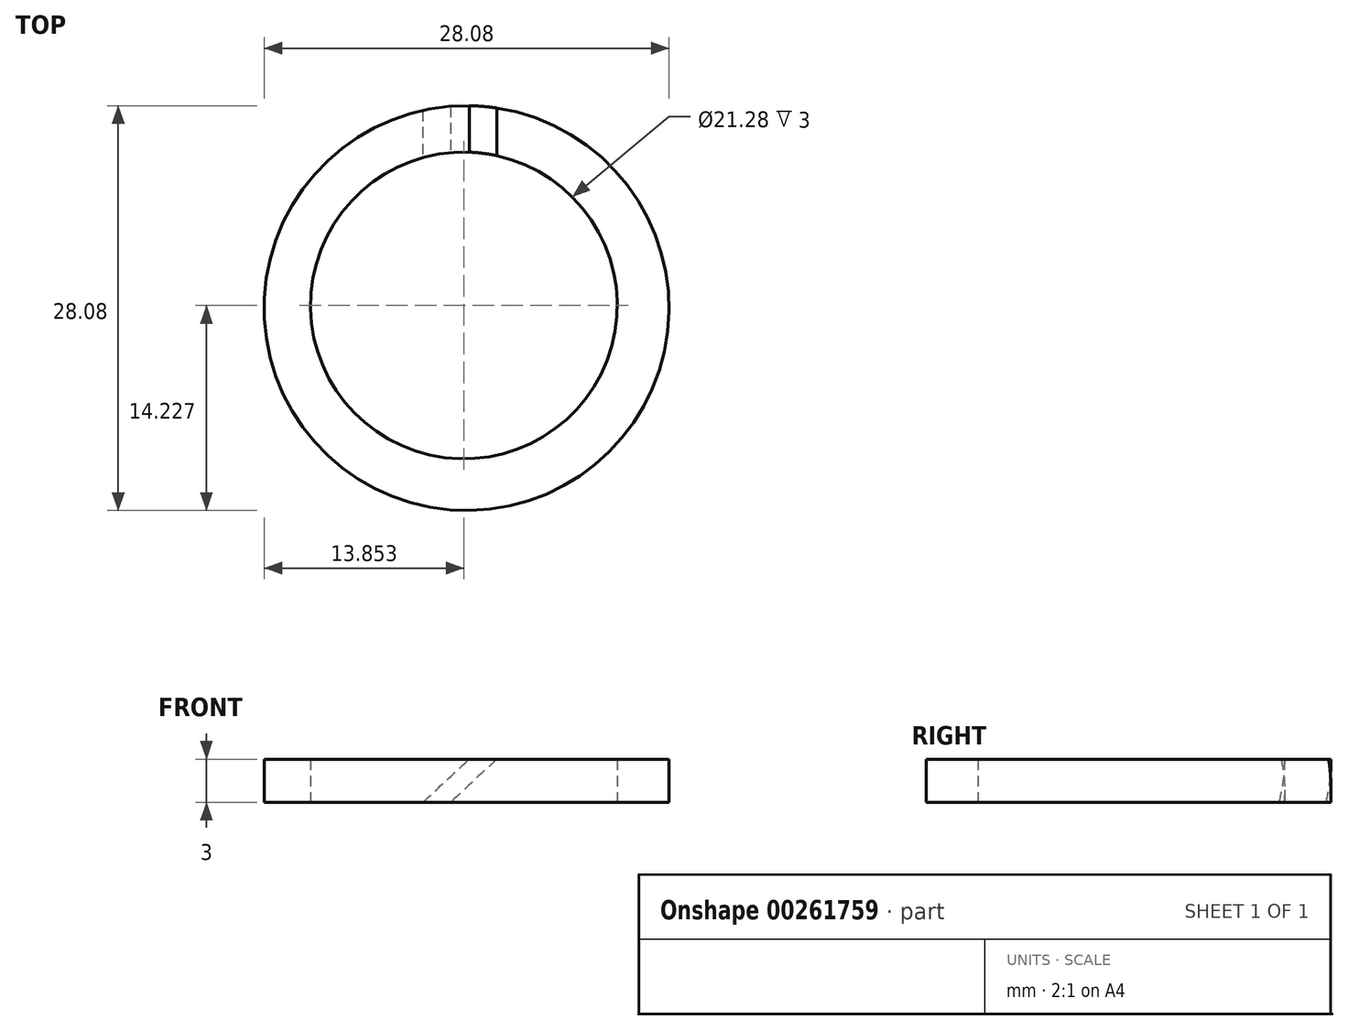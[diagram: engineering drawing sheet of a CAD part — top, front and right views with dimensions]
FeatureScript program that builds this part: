
annotation { "Feature Type Name" : "Feature", "Feature Type Description" : "" }
export const myFeature = defineFeature(function(context is Context, id is Id, definition is map)
    precondition{}
    {
        {
            var Q0;
            Q0=qCreatedBy(makeId("Top.planeOp"),FACE);
            var sketch = newSketch(context, id + "F0", { "sketchPlane" : qUnion([Q0])});
            skCircle(sketch, "E0", {"center": v(0, 0) * mm, "radius": 14.04 * mm});
            skCircle(sketch, "E1", {"center": v(-0.19, 0.19) * mm, "radius": 10.64 * mm});
            skSolve(sketch);
        }
        {
            var Q0;
            Q0 = qSketchRegion(id + "F0", true);
            extrude(context, id + "F1", {"entities" : qUnion([Q0]), "depth" : 3 * mm});
        }
        {
            var Q0;
            Q0=qCreatedBy(makeId("Front.planeOp"),FACE);
            var sketch = newSketch(context, id + "F2", { "sketchPlane" : qUnion([Q0])});
            skLineSegment(sketch, "E2", {"start": v(-3.03, 0) * mm, "end": v(1.62, 4.34) * mm});
            skLineSegment(sketch, "E3", {"start": v(1.62, 4.34) * mm, "end": v(3.53, 4.34) * mm});
            skLineSegment(sketch, "E4", {"start": v(3.53, 4.34) * mm, "end": v(-1.12, 0) * mm});
            skLineSegment(sketch, "E5", {"start": v(-1.12, 0) * mm, "end": v(-3.03, 0) * mm});
            skSolve(sketch);
        }
        {
            var Q0;
            Q0=makeQuery(id+"F2.imprint","IMPRINT",FACE,{"disambiguationData":[TD([[makeQuery(id+"F2.imprint","IMPRINT",EDGE,{"derivedFrom":sQuery(id+"F2.wireOp",EDGE,"E2")}),-1.0]])]});
            extrude(context, id + "F3", {"entities" : qUnion([Q0]), "operationType" : NewBodyOperationType.REMOVE, "oppositeDirection" : true, "depth" : 25 * mm});
        }
    });
